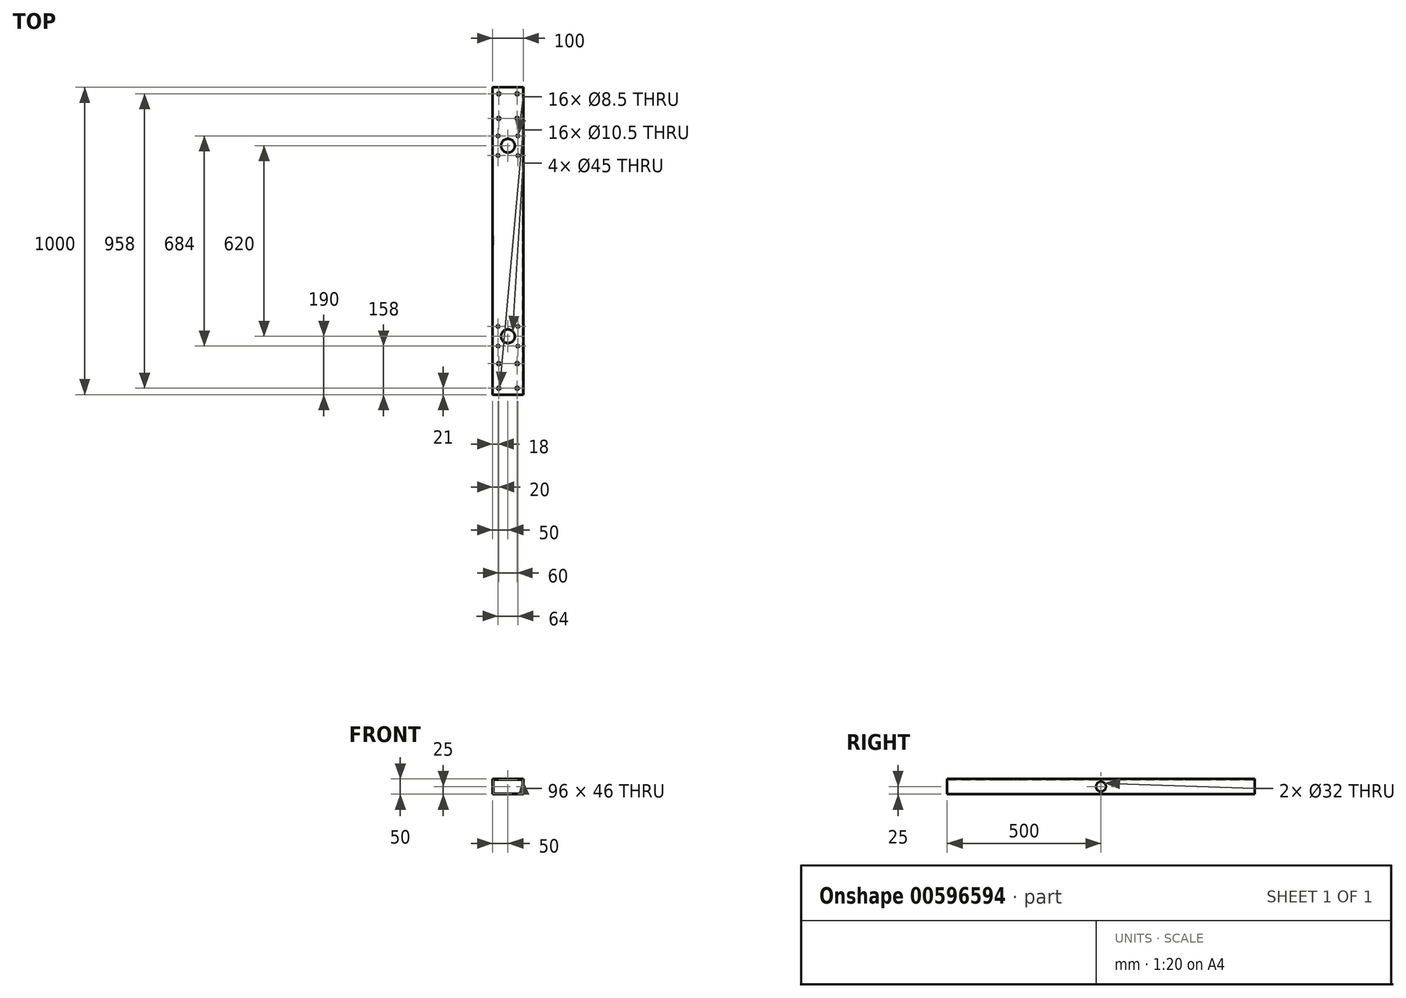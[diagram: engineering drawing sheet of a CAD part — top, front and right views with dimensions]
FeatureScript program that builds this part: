
annotation { "Feature Type Name" : "Feature", "Feature Type Description" : "" }
export const myFeature = defineFeature(function(context is Context, id is Id, definition is map)
    precondition{}
    {
        {
            var Q0;
            Q0=qCreatedBy(makeId("Front.planeOp"),FACE);
            var sketch = newSketch(context, id + "F0", { "sketchPlane" : qUnion([Q0])});
            skLineSegment(sketch, "E0.bottom", {"start": v(0, 0) * mm, "end": v(100, 0) * mm});
            skLineSegment(sketch, "E0.top", {"start": v(0, 50) * mm, "end": v(100, 50) * mm});
            skLineSegment(sketch, "E0.left", {"start": v(0, 0) * mm, "end": v(0, 50) * mm});
            skLineSegment(sketch, "E0.right", {"start": v(100, 0) * mm, "end": v(100, 50) * mm});
            skLineSegment(sketch, "E1.0", {"start": v(2, 48) * mm, "end": v(98, 48) * mm});
            skLineSegment(sketch, "E2.0", {"start": v(2, 2) * mm, "end": v(2, 48) * mm});
            skLineSegment(sketch, "E3.0", {"start": v(2, 2) * mm, "end": v(98, 2) * mm});
            skLineSegment(sketch, "E4.0", {"start": v(98, 2) * mm, "end": v(98, 48) * mm});
            skSolve(sketch);
        }
        {
            var Q0;
            Q0 = qSketchRegion(id + "F0", true);
            extrude(context, id + "F1", {"entities" : qUnion([Q0]), "depth" : 1000 * mm, "offsetDistance" : 25 * mm});
        }
        {
            var Q0;
            Q0=makeQuery(id+"F1.opExtrude","SWEPT_FACE",FACE,{"disambiguationData":[OSD([sQuery(id+"F0.wireOp",EDGE,"E0.top")])]});
            var sketch = newSketch(context, id + "F2", { "sketchPlane" : qUnion([Q0])});
            skLineSegment(sketch, "E5", {"start": v(0, -500) * mm, "end": v(100, -500) * mm, "construction": true});
            skLineSegment(sketch, "E6.0", {"start": v(0, -810) * mm, "end": v(100, -810) * mm, "construction": true});
            skLineSegment(sketch, "E7.0", {"start": v(0, -190) * mm, "end": v(100, -190) * mm, "construction": true});
            skCircle(sketch, "E8", {"center": v(50, -810) * mm, "radius": 22.5 * mm});
            skCircle(sketch, "E9", {"center": v(50, -190) * mm, "radius": 22.5 * mm});
            skSolve(sketch);
        }
        {
            var Q0;
            Q0 = qSketchRegion(id + "F2", true);
            extrude(context, id + "F3", {"entities" : qUnion([Q0]), "operationType" : NewBodyOperationType.REMOVE, "endBound" : BoundingType.THROUGH_ALL, "oppositeDirection" : true, "depth" : 25 * mm, "offsetDistance" : 25 * mm});
        }
        {
            var Q0;
            Q0=makeQuery(id+"F1.opExtrude","SWEPT_FACE",FACE,{"disambiguationData":[OSD([sQuery(id+"F0.wireOp",EDGE,"E0.top")])]});
            var sketch = newSketch(context, id + "F4", { "sketchPlane" : qUnion([Q0])});
            skLineSegment(sketch, "E10.bottom", {"start": v(82, -842) * mm, "end": v(18, -842) * mm, "construction": true});
            skLineSegment(sketch, "E10.top", {"start": v(82, -778) * mm, "end": v(18, -778) * mm, "construction": true});
            skLineSegment(sketch, "E10.left", {"start": v(82, -842) * mm, "end": v(82, -778) * mm, "construction": true});
            skLineSegment(sketch, "E10.right", {"start": v(18, -842) * mm, "end": v(18, -778) * mm, "construction": true});
            skPoint(sketch, "E11", {"position": v(18, -842) * mm});
            skPoint(sketch, "E12", {"position": v(18, -778) * mm});
            skPoint(sketch, "E13", {"position": v(82, -778) * mm});
            skPoint(sketch, "E14", {"position": v(82, -842) * mm});
            skPoint(sketch, "E15", {"position": v(20, -979) * mm});
            skPoint(sketch, "E16.0.1.0", {"position": v(20, -899) * mm});
            skPoint(sketch, "E16.1.0.0", {"position": v(80, -979) * mm});
            skPoint(sketch, "E16.1.1.0", {"position": v(80, -899) * mm});
            skLineSegment(sketch, "E16.direction1", {"start": v(20, -979) * mm, "end": v(80, -979) * mm, "construction": true});
            skLineSegment(sketch, "E16.direction2", {"start": v(20, -979) * mm, "end": v(20, -899) * mm, "construction": true});
            skLineSegment(sketch, "E17", {"start": v(0, -500) * mm, "end": v(100, -500) * mm, "construction": true});
            skPoint(sketch, "E18.MirrorP", {"position": v(18, -222) * mm});
            skPoint(sketch, "E19.MirrorP", {"position": v(18, -158) * mm});
            skPoint(sketch, "E20.MirrorP", {"position": v(82, -158) * mm});
            skPoint(sketch, "E21.MirrorP", {"position": v(82, -222) * mm});
            skPoint(sketch, "E22.MirrorP", {"position": v(80, -101) * mm});
            skPoint(sketch, "E23.MirrorP", {"position": v(20, -101) * mm});
            skPoint(sketch, "E24.MirrorP", {"position": v(20, -21) * mm});
            skPoint(sketch, "E25.MirrorP", {"position": v(80, -21) * mm});
            skSolve(sketch);
        }
        {
            var Q0;
            Q0=sQuery(id+"F4.wireOp",VERTEX,"E11");
            var Q1;
            Q1=sQuery(id+"F4.wireOp",VERTEX,"E12");
            var Q2;
            Q2=sQuery(id+"F4.wireOp",VERTEX,"E13");
            var Q3;
            Q3=sQuery(id+"F4.wireOp",VERTEX,"E14");
            var Q4;
            Q4=sQuery(id+"F4.wireOp",VERTEX,"E18.MirrorP");
            var Q5;
            Q5=sQuery(id+"F4.wireOp",VERTEX,"E19.MirrorP");
            var Q6;
            Q6=sQuery(id+"F4.wireOp",VERTEX,"E20.MirrorP");
            var Q7;
            Q7=sQuery(id+"F4.wireOp",VERTEX,"E21.MirrorP");
            var Q8;
            Q8=makeQuery(id+"F1.opExtrude","SWEPT_BODY",BODY,{"disambiguationData":[OSD([sQuery(id+"F0.wireOp",EDGE,"E0.bottom"),sQuery(id+"F0.wireOp",EDGE,"E0.top"),sQuery(id+"F0.wireOp",EDGE,"E0.left"),sQuery(id+"F0.wireOp",EDGE,"E0.right"),sQuery(id+"F0.wireOp",EDGE,"E1.0"),sQuery(id+"F0.wireOp",EDGE,"E2.0"),sQuery(id+"F0.wireOp",EDGE,"E3.0"),sQuery(id+"F0.wireOp",EDGE,"E4.0")])]});
            hole(context, id + "F5", {"style" : HoleStyle.SIMPLE, "endStyle" : HoleEndStyle.THROUGH, "holeDiameter" : 8.5 * mm, "majorDiameter" : 5 * mm, "isTappedThrough" : true, "tappedDepth" : 12 * mm, "tapClearance" : 3, "startFromSketch" : true, "locations" : qUnion([Q0, Q1, Q2, Q3, Q4, Q5, Q6, Q7]), "scope" : qUnion([Q8])});
        }
        {
            var Q0;
            Q0=sQuery(id+"F4.wireOp",VERTEX,"E23.MirrorP");
            var Q1;
            Q1=sQuery(id+"F4.wireOp",VERTEX,"E24.MirrorP");
            var Q2;
            Q2=sQuery(id+"F4.wireOp",VERTEX,"E25.MirrorP");
            var Q3;
            Q3=sQuery(id+"F4.wireOp",VERTEX,"E22.MirrorP");
            var Q4;
            Q4=sQuery(id+"F4.wireOp",VERTEX,"E16.0.1.0");
            var Q5;
            Q5=sQuery(id+"F4.wireOp",VERTEX,"E15");
            var Q6;
            Q6=sQuery(id+"F4.wireOp",VERTEX,"E16.1.0.0");
            var Q7;
            Q7=sQuery(id+"F4.wireOp",VERTEX,"E16.1.1.0");
            var Q8;
            Q8=makeQuery(id+"F1.opExtrude","SWEPT_BODY",BODY,{"disambiguationData":[OSD([sQuery(id+"F0.wireOp",EDGE,"E0.bottom"),sQuery(id+"F0.wireOp",EDGE,"E0.top"),sQuery(id+"F0.wireOp",EDGE,"E0.left"),sQuery(id+"F0.wireOp",EDGE,"E0.right"),sQuery(id+"F0.wireOp",EDGE,"E1.0"),sQuery(id+"F0.wireOp",EDGE,"E2.0"),sQuery(id+"F0.wireOp",EDGE,"E3.0"),sQuery(id+"F0.wireOp",EDGE,"E4.0")])]});
            hole(context, id + "F6", {"style" : HoleStyle.SIMPLE, "endStyle" : HoleEndStyle.THROUGH, "holeDiameter" : 10.5 * mm, "majorDiameter" : 5 * mm, "isTappedThrough" : true, "tappedDepth" : 12 * mm, "tapClearance" : 3, "startFromSketch" : true, "locations" : qUnion([Q0, Q1, Q2, Q3, Q4, Q5, Q6, Q7]), "scope" : qUnion([Q8])});
        }
        {
            var Q0;
            Q0=makeQuery(id+"F1.opExtrude","SWEPT_FACE",FACE,{"disambiguationData":[OSD([sQuery(id+"F0.wireOp",EDGE,"E0.right")])]});
            var sketch = newSketch(context, id + "F7", { "sketchPlane" : qUnion([Q0])});
            skCircle(sketch, "E26", {"center": v(-500, 25) * mm, "radius": 16 * mm});
            skPoint(sketch, "E26.centerSnap0", {"position": v(0, 25) * mm});
            skPoint(sketch, "E26.centerSnap1", {"position": v(-500, 50) * mm});
            skSolve(sketch);
        }
        {
            var Q0;
            Q0 = qSketchRegion(id + "F7", true);
            extrude(context, id + "F8", {"entities" : qUnion([Q0]), "operationType" : NewBodyOperationType.REMOVE, "endBound" : BoundingType.THROUGH_ALL, "oppositeDirection" : true, "depth" : 25 * mm, "offsetDistance" : 25 * mm});
        }
    });
